# Revit family: P500223-031
name_source: partatom
category: Lighting Fixtures
revit_build: Autodesk Revit 2014 (Build: 20130308_1515(x64)
units: mm (PartAtom-declared; Revit-internal decimal feet)

## types (1)
- P500223-031
    Apparent Load = 60 VA
    Assembly Code = D5020200
    Color Filter = 16777215
    Connector Description = Lighting Connector
    Default Elevation = 48"
    Description = The Bonn Collection One-Light Black Mini-Pendant personifies an industrial vintage vibe sure to create an unforgettable lighting experience. Smooth metal bars coated in a beautiful matte black finish curve to form a simple, open-cage light fixture. From the bottom of the sleek center stem, a single light base appears to drop and gives an extra touch of refined visual interest.
    Diameter = 7"
    Dimming Lamp Color Temperature Shift = <None>
    Fixture distribution = Direct
    Glass = Hubbell - Glass
    Height = 14 7/8"
    Housing Material = Paint - Hubbell - Metallic Bronze Textured
    Lamp = A-19
    Load Classification = Lighting
    Manufacturer = Progress Lighting
    Model = P500223-031
    Photometric Web File = generic
    Power Factor = 1
    Product Documentation Link = https://hubbellcdn.com
    Product Link = https://www.hubbell.com
    Specifications = From the bottom of the sleek center column, a light base appears to gracefully drip down and provides an extra touch of refined visual interest.
Smooth metal bars curve to form a simple, open-cage design.
The mini-pendant is coated in a beautiful matte black finish for a classic look.
Ideal for any foyer, dining room, or kitchen.
A great vintage choice for urban industrial, vintage, electric, farmhouse, and rustic interiors.
Measures 7-inch width by 14-7/8-inch height.
Uses one medium base bulb or vintage T10 bulb that is sold separately (60w max - LED or incandescent).
Able to be fully dimmable with dimmable bulbs.
Includes installation instructions and mounting hardware.
Progress Lighting products are designed for exceptional quality, reliability, and functionality.
    Tilt Angle = 60.00°
    URL = https://www.hubbell.com
    Voltage = 120 V
    Warranty = 5 years Warranty
    Wattage Comments = 60W
    Watts = 60 W

## geometry (parser evidence)
native form markers: Sweep x6
no freeform markers — native parametric forms only
